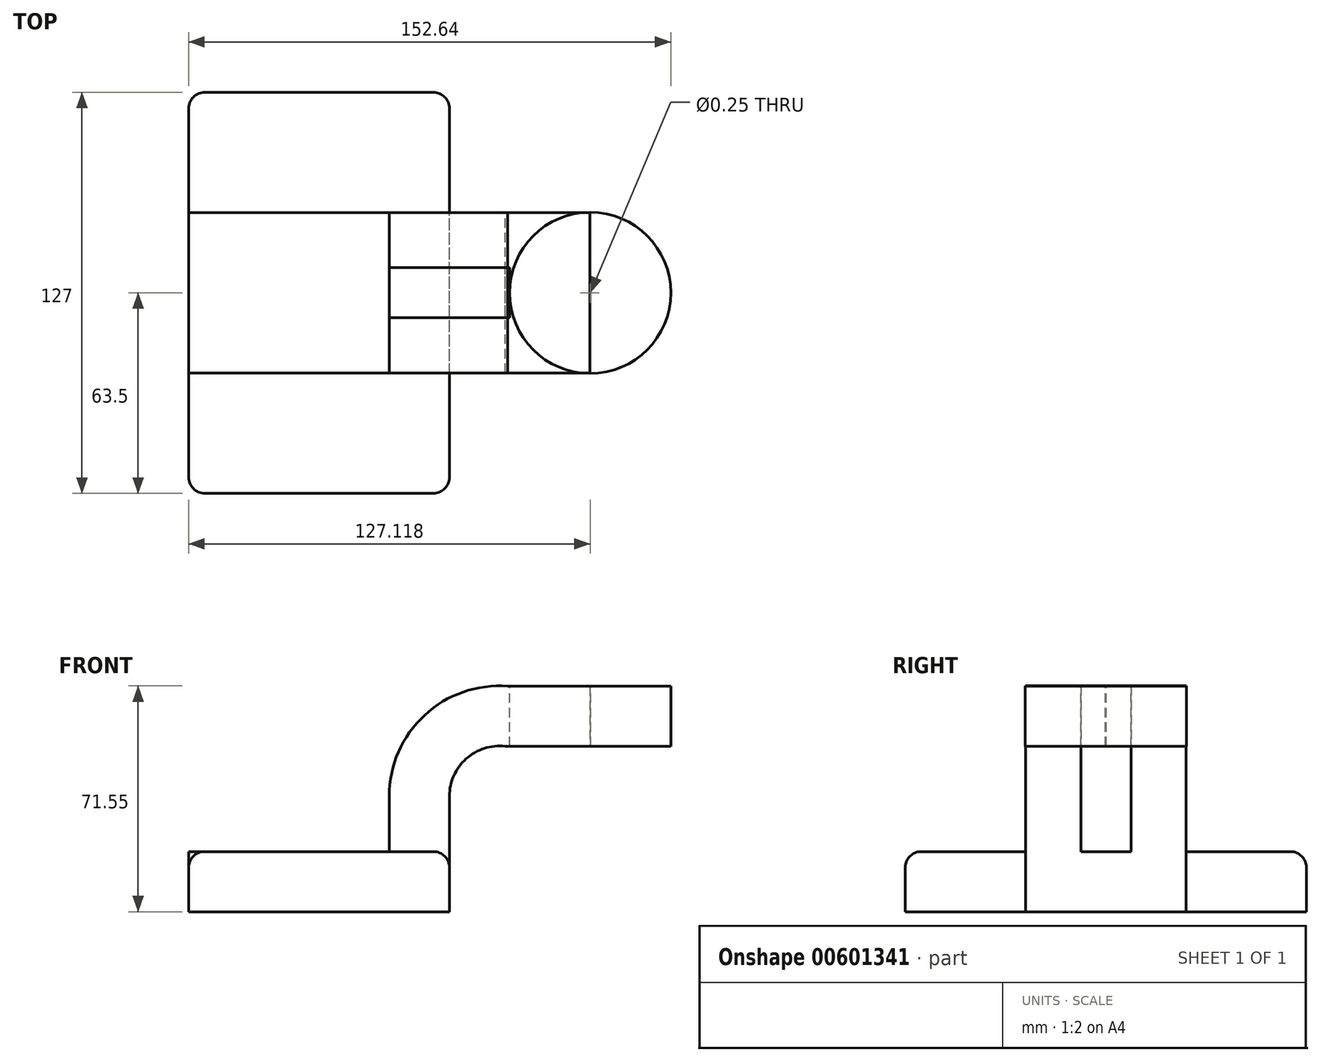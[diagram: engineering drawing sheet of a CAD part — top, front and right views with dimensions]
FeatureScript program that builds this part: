
annotation { "Feature Type Name" : "Feature", "Feature Type Description" : "" }
export const myFeature = defineFeature(function(context is Context, id is Id, definition is map)
    precondition{}
    {
        {
            var Q0;
            Q0=qCreatedBy(makeId("Front.planeOp"),FACE);
            var sketch = newSketch(context, id + "F0", { "sketchPlane" : qUnion([Q0])});
            skLineSegment(sketch, "E0.bottom", {"start": v(-41.28, -9.53) * mm, "end": v(41.28, -9.53) * mm});
            skLineSegment(sketch, "E0.top", {"start": v(-41.28, 9.53) * mm, "end": v(41.28, 9.53) * mm});
            skLineSegment(sketch, "E0.left", {"start": v(-41.28, -9.53) * mm, "end": v(-41.28, 9.53) * mm});
            skLineSegment(sketch, "E0.right", {"start": v(41.28, -9.53) * mm, "end": v(41.28, 9.53) * mm});
            skPoint(sketch, "E0.middle", {"position": v(0, 0) * mm});
            skLineSegment(sketch, "E1.bottom", {"start": v(60.32, 38.1) * mm, "end": v(111.12, 38.1) * mm});
            skLineSegment(sketch, "E1.top", {"start": v(60.32, 66.67) * mm, "end": v(111.12, 66.67) * mm});
            skLineSegment(sketch, "E1.left", {"start": v(60.32, 38.1) * mm, "end": v(60.32, 66.67) * mm});
            skLineSegment(sketch, "E1.right", {"start": v(111.12, 38.1) * mm, "end": v(111.12, 66.67) * mm});
            skPoint(sketch, "E1.middle", {"position": v(85.72, 52.39) * mm});
            skLineSegment(sketch, "E2", {"start": v(41.28, 9.53) * mm, "end": v(41.28, 27.1) * mm});
            skArc(sketch, "E3", {"start": v(41.28, 27.1) * mm, "mid": v(46.57, 38.93) * mm, "end": v(58.92, 42.88) * mm});
            skLineSegment(sketch, "E4", {"start": v(58.92, 42.88) * mm, "end": v(85.72, 42.88) * mm});
            skLineSegment(sketch, "E5.0", {"start": v(59.77, 61.93) * mm, "end": v(85.85, 61.93) * mm});
            skArc(sketch, "E5.1", {"start": v(22.22, 27.1) * mm, "mid": v(33.4, 52.7) * mm, "end": v(59.77, 61.93) * mm});
            skLineSegment(sketch, "E5.2", {"start": v(22.22, 9.53) * mm, "end": v(22.22, 27.1) * mm});
            skLineSegment(sketch, "E6", {"start": v(85.85, 61.93) * mm, "end": v(85.73, 42.88) * mm});
            skLineSegment(sketch, "E7", {"start": v(85.85, 66.67) * mm, "end": v(85.85, 38.1) * mm});
            skFitSpline(sketch, "E8", {"points": [v(-41.28, 9.52) * mm, v(59.77, 61.93) * mm], "startDerivative": vector(52.62, 123.26) * mm, "endDerivative": vector(103.12, -8.75) * mm});
            skLineSegment(sketch, "E9", {"start": v(85.72, 66.67) * mm, "end": v(85.72, 38.1) * mm});
            skSolve(sketch);
        }
        {
            var Q0;
            Q0=makeQuery(id+"F0.imprint","IMPRINT",FACE,{"disambiguationData":[TD([[makeQuery(id+"F0.imprint","IMPRINT",EDGE,{"derivedFrom":sQuery(id+"F0.wireOp",EDGE,"E0.bottom")}),1.0]])]});
            extrude(context, id + "F1", {"entities" : qUnion([Q0]), "endBound" : BoundingType.SYMMETRIC, "depth" : 127 * mm, "offsetDistance" : 25.4 * mm});
        }
        {
            var Q0;
            Q0=makeQuery(id+"F0.imprint","IMPRINT",FACE,{"disambiguationData":[TD([[makeQuery(id+"F0.imprint","IMPRINT",EDGE,{"derivedFrom":sQuery(id+"F0.wireOp",EDGE,"E0.bottom")}),1.0]])]});
            var Q1;
            {var subQ1=sQuery(id+"F0.wireOp",EDGE,"E2");Q1=makeQuery(id+"F0.imprint","IMPRINT",FACE,{"disambiguationData":[TD([[makeQuery(id+"F0.imprint","IMPRINT",EDGE,{"derivedFrom":subQ1}),1.0]])]});}
            var Q2;
            {var subQ0=sQuery(id+"F0.wireOp",EDGE,"E4");var subQ1=sQuery(id+"F0.wireOp",EDGE,"E1.left");var subQ2=makeQuery(id+"F0.imprint","INTERSECT",VERTEX,{"derivedFrom":[subQ1,subQ0]});Q2=makeQuery(id+"F0.imprint","IMPRINT",FACE,{"disambiguationData":[TD([[makeQuery(id+"F0.imprint","IMPRINT",EDGE,{"disambiguationData":[TD([[subQ2,-1.0]])],"derivedFrom":subQ1}),-1.0]])]});}
            extrude(context, id + "F2", {"entities" : qUnion([Q0, Q1, Q2]), "endBound" : BoundingType.SYMMETRIC, "depth" : 50.8 * mm, "offsetDistance" : 25.4 * mm});
        }
        {
            var Q0;
            Q0=makeQuery(id+"F0.imprint","IMPRINT",FACE,{"disambiguationData":[TD([[makeQuery(id+"F0.imprint","IMPRINT",EDGE,{"derivedFrom":sQuery(id+"F0.wireOp",EDGE,"E5.1")}),1.0]])]});
            extrude(context, id + "F3", {"entities" : qUnion([Q0]), "endBound" : BoundingType.SYMMETRIC, "depth" : 15.88 * mm, "offsetDistance" : 25.4 * mm});
        }
        {
            var Q0;
            {var subQ0=sQuery(id+"F0.wireOp",EDGE,"E4");var subQ1=sQuery(id+"F0.wireOp",EDGE,"E1.left");var subQ2=makeQuery(id+"F0.imprint","INTERSECT",VERTEX,{"derivedFrom":[subQ1,subQ0]});Q0=makeQuery(id+"F0.imprint","IMPRINT",FACE,{"disambiguationData":[TD([[makeQuery(id+"F0.imprint","IMPRINT",EDGE,{"disambiguationData":[TD([[subQ2,-1.0]])],"derivedFrom":subQ1}),-1.0]])]});}
            var Q1;
            Q1=sQuery(id+"F0.wireOp",EDGE,"E7");
            revolve(context, id + "F4", {"entities" : qUnion([Q0]), "axis" : qUnion([Q1]), "revolveType" : RevolveType.FULL});
        }
        {
            var Q0;
            Q0=makeQuery(id+"F1.opExtrude","CAP_EDGE",EDGE,{"disambiguationData":[OSD([sQuery(id+"F0.wireOp",EDGE,"E0.right")])],"isStart":false});
            var Q1;
            Q1=makeQuery(id+"F1.opExtrude","CAP_EDGE",EDGE,{"disambiguationData":[OSD([sQuery(id+"F0.wireOp",EDGE,"E0.left")])],"isStart":false});
            var Q2;
            Q2=makeQuery(id+"F1.opExtrude","CAP_EDGE",EDGE,{"disambiguationData":[OSD([sQuery(id+"F0.wireOp",EDGE,"E0.right")])],"isStart":true});
            var Q3;
            Q3=makeQuery(id+"F1.opExtrude","CAP_EDGE",EDGE,{"disambiguationData":[OSD([sQuery(id+"F0.wireOp",EDGE,"E0.left")])],"isStart":true});
            var Q4;
            Q4=makeQuery(id+"F1.opExtrude","CAP_EDGE",EDGE,{"disambiguationData":[OSD([sQuery(id+"F0.wireOp",EDGE,"E0.top")])],"isStart":true});
            var Q5;
            Q5=makeQuery(id+"F1.opExtrude","SWEPT_EDGE",EDGE,{"disambiguationData":[OSD([sQuery(id+"F0.wireOp",EDGE,"E0.top"),sQuery(id+"F0.wireOp",EDGE,"E0.left"),sQuery(id+"F0.wireOp",EDGE,"E8")])]});
            var Q6;
            Q6=makeQuery(id+"F1.opExtrude","SWEPT_EDGE",EDGE,{"disambiguationData":[OSD([sQuery(id+"F0.wireOp",EDGE,"E0.top"),sQuery(id+"F0.wireOp",EDGE,"E0.right"),sQuery(id+"F0.wireOp",EDGE,"E2")])]});
            var Q7;
            Q7=makeQuery(id+"F1.opExtrude","CAP_EDGE",EDGE,{"disambiguationData":[OSD([sQuery(id+"F0.wireOp",EDGE,"E0.top")])],"isStart":false});
            fillet(context, id + "F5", {"entities" : qUnion([Q0, Q1, Q2, Q3, Q4, Q5, Q6, Q7]), "radius" : 5.08 * mm, "tangentPropagation" : true, "allowEdgeOverflow" : false});
        }
    });
